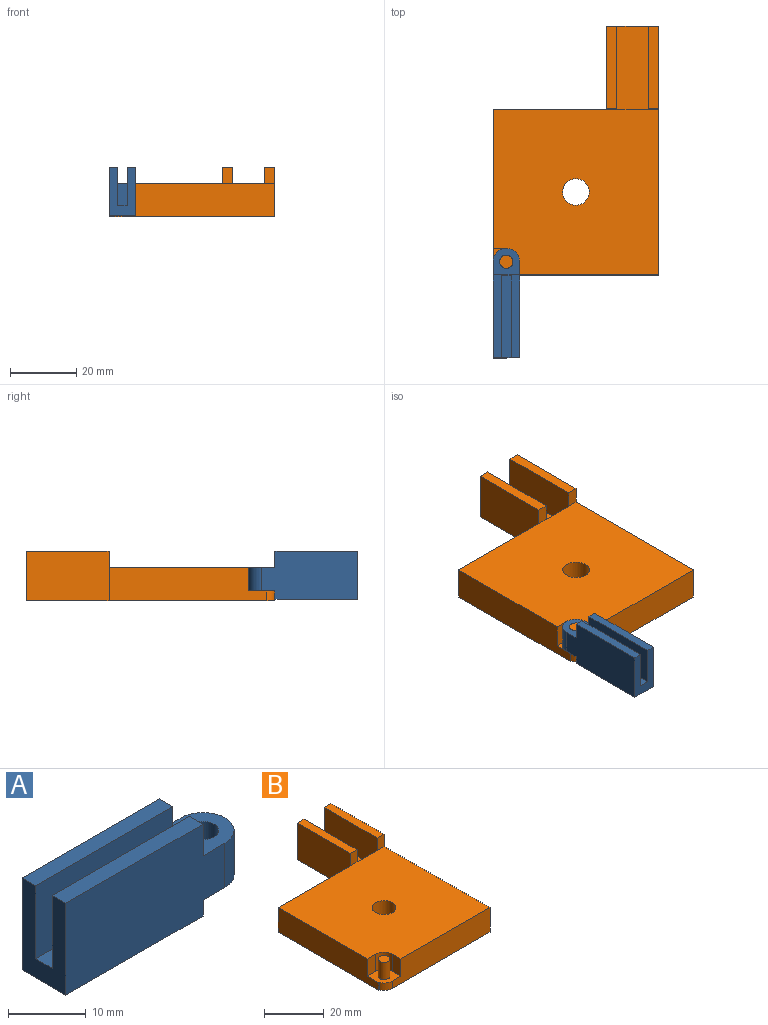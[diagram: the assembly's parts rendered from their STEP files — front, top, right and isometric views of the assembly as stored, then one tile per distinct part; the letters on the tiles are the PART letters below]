
ASSEMBLY  parts=2 mates=1
PART A: 17 faces, bbox 33x8x14.5 mm
  f0: plane 8x8mm, normal (0,0,1), area 44.6mm2, adj f1,f3,f6,f8,f9,f13,f15
  f1: plane 29x14.5mm, normal (0,1,0), area 390.5mm2, adj f0,f2,f3,f4,f11,f12,f13,f14
  f2: plane 25x8mm, normal (0,0,-1), area 200mm2, adj f1,f4,f9,f11
  f3: cylinder r=4mm len=8mm, axis (0,0,-1), area 88mm2, adj f0,f1,f9,f12
  f4: plane 14.5x8mm, normal (-1,0,0), area 81.5mm2, adj f1,f2,f5,f7,f9,f10,f14,f16
  f5: plane 25x11.5mm, normal (0,-1,0), area 287.5mm2, adj f4,f6,f10,f13,f14
  f6: plane 6.5x3mm, normal (-1,0,0), area 19.5mm2, adj f0,f5,f7,f10
  f7: plane 25x11.5mm, normal (0,1,0), area 287.5mm2, adj f4,f6,f10,f15,f16
  f8: cylinder r=2mm len=7mm, axis (0,0,-1), area 88mm2, adj f0,f12
  f9: plane 29x14.5mm, normal (0,-1,0), area 390.5mm2, adj f0,f2,f3,f4,f11,f12,f15,f16
  f10: plane 25x3mm, normal (0,0,1), area 75mm2, adj f4,f5,f6,f7
  f11: plane 8x2.5mm, normal (1,0,0), area 20mm2, adj f1,f2,f9,f12
  f12: plane 8x8mm, normal (0,0,-1), area 44.6mm2, adj f1,f3,f8,f9,f11
  f13: plane 5x2.5mm, normal (1,0,0), area 12.5mm2, adj f0,f1,f5,f14
  f14: plane 25x2.5mm, normal (0,0,1), area 62.5mm2, adj f1,f4,f5,f13
  f15: plane 5x2.5mm, normal (1,0,0), area 12.5mm2, adj f0,f7,f9,f16
  f16: plane 25x2.5mm, normal (0,0,1), area 62.5mm2, adj f4,f7,f9,f15
PART B: 25 faces, bbox 50x75x15 mm
  f0: plane 9.53x7mm, normal (0,1,0), area 66.7mm2, adj f1,f15,f19,f22
  f1: plane 25x9.53mm, normal (0,0,1), area 238.1mm2, adj f0,f7,f19,f22
  f2: plane 8x8mm, normal (0,0,1), area 44.7mm2, adj f3,f4,f8,f9,f12,f13,f14,f16
  f3: cylinder r=4mm len=3.71mm, axis (0,0,-1), area 14.2mm2, adj f2,f4,f9,f11
  f4: plane 46x10mm, normal (0,-1,0), area 432mm2, adj f2,f3,f5,f11,f14,f15
  f5: plane 75x15mm, normal (1,0,0), area 875mm2, adj f4,f7,f11,f15,f18,f20
  f6: plane 34.13x10mm, normal (0,1,0), area 341.3mm2, adj f8,f11,f15,f23
  f7: plane 15.88x15mm, normal (0,1,0), area 123.8mm2, adj f1,f5,f11,f19,f20,f22,f23,f24
  f8: plane 47.5x10mm, normal (-1,0,0), area 436.5mm2, adj f2,f6,f9,f11,f12,f15
  f9: plane 3x0.29mm, normal (0,-1,0), area 0.9mm2, adj f2,f3,f8,f11
  f10: cylinder r=4mm len=10mm, axis (0,0,-1), area 251.3mm2, adj f11,f15
  f11: plane 75x50mm, normal (0,0,-1), area 2843.3mm2, adj f3,f4,f5,f6,f7,f8,f9,f10
  f12: plane 7x4mm, normal (0,-1,0), area 28mm2, adj f2,f8,f13,f15
  f13: cylinder r=4mm len=7mm, axis (0,0,-1), area 44mm2, adj f2,f12,f14,f15
  f14: plane 7x4mm, normal (-1,0,0), area 28mm2, adj f2,f4,f13,f15
  f15: plane 50x50mm, normal (0,0,1), area 2389.2mm2, adj f0,f4,f5,f6,f8,f10,f12,f13
  f16: cylinder r=2mm len=7mm, axis (0,0,-1), area 88mm2, adj f2,f17
  f17: plane 4x4mm, normal (0,0,1), area 12.6mm2, adj f16
  f18: plane 5x3.18mm, normal (0,-1,0), area 15.9mm2, adj f5,f15,f19,f20
  f19: plane 25x12mm, normal (-1,0,0), area 300mm2, adj f0,f1,f7,f18,f20
  f20: plane 25x3.18mm, normal (0,0,1), area 79.4mm2, adj f5,f7,f18,f19
  f21: plane 5x3.18mm, normal (0,-1,0), area 15.9mm2, adj f15,f22,f23,f24
  f22: plane 25x12mm, normal (1,0,0), area 300mm2, adj f0,f1,f7,f21,f24
  f23: plane 25x15mm, normal (-1,0,0), area 375mm2, adj f6,f7,f11,f21,f24
  f24: plane 25x3.18mm, normal (0,0,1), area 79.4mm2, adj f7,f21,f22,f23
PLACE A rot(axis=(0,0,1),90deg) t=(-63.99,8.47,-13.44)mm
PLACE B t=(-21.99,8.47,-13.94)mm fixed
MATE revolute A.f3 <-> B.f3  axis (0,0,-1) through (-42.99,-12.53,-10.94)mm
